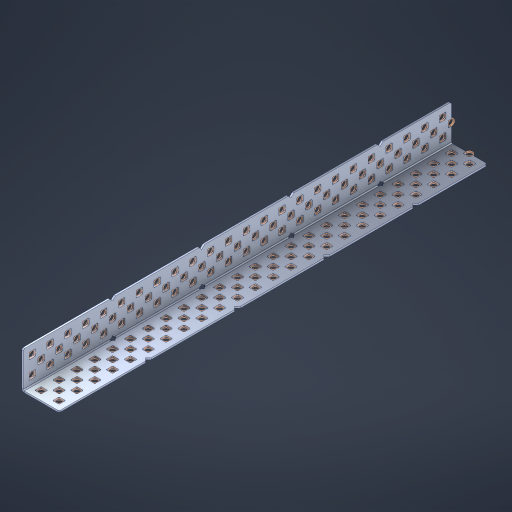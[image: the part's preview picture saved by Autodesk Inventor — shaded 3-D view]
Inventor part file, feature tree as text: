
AUTODESK INVENTOR PART (.ipt)
format: ipt  version: 2023 (Build 270158000, 158)  size: 1,733,120 bytes
history: native  units: in
note: dims shown in document units (in); Inventor stores cm internally (conversion verified against a paired STEP export)
features: other x150, extrude x142, sheet_metal_op x8, sketch x7, pattern_linear x2, mirror x1, chamfer x1
ambient origin geometry x8: Origin, YZ Plane, XZ Plane, XY Plane, X Axis, Y Axis, Z Axis, Center Point
bodies: Solid1 (feature_tree), Body (feature_tree)
feature tree (311):
  sheet_metal_op  "Flanges"
  sheet_metal_op  "Body Pattern"
  pattern_linear  "Center Pattern"  Spacing1=1.0in  [1 undecoded]
  other  "Arc Length"
  pattern_linear  "Notch Pattern"  Spacing1=0.1875in  [1 undecoded]
  other  "Diagonal Plane"
  mirror  "Everything Mirrored"
  chamfer  "End Chamfer"
  sketch  "Sketch1"  dims[d0=1.0in]
  other  "Plate1"
  sketch  "Sketch2"  dims[d1=12.0in]
  other  "Plate2"
  sheet_metal_op  "Bend1"
  sheet_metal_op  "Corner1"
  sketch  "Sketch8"  dims[d2=0.0469in]
  sketch  "Sketch9"  dims[d3=0.0469in]
  other  "Srf91"
  sheet_metal_op  "Body Pattern Sketch"
  other  "Srf92"
  sketch  "Sketch13"  dims[d4=0.0234in]
  sketch  "Sketch15"  dims[d5=0.0938in]
  sketch  "Sketch16"  dims[d6=0.0469in d7=1.0in d8=90.0deg d9=0.0312in d10=0.1875in d11=0.0469in d12=0.0469in d49=0.182in d50=0.02in d52=0.25in d53=0.0469in d54=0.0in d55=0.172in d56=1.0in d57=0.0in d60=9.4488in d62=0.5in d63=0.7874in d65=0.5in d85=0.1473in d86=0.1659in d89=0.0469in d90=0.0in d91=0.04in d92=0.0491in d95=2.5in d96=0.04in d97=0.25in d98=45.0deg d99=0.25in d106=0.182in d107=0.02in d108=0.5in d110=0.0469in d111=0.0in d112=0.172in d113=0.5in d114=0.0in d117=0.5in d123=0.25in d125=0.25in d126=0.0491in d127=0.1227in d128=0.08in d129=0.04in d130=2.5in]
  other  "Srf786"
  other  "Srf856"
  other  "Srf857"
  other  "Srf858"
  other  "Srf859"
  other  "Srf860"
  other  "Srf861"
  other  "Srf889"
  other  "Srf890"
  other  "Srf891"
  other  "Srf1275"
  other  "Srf1276"
  other  "Srf1278"
  other  "Srf1279"
  other  "Srf1280"
  other  "Srf1281"
  other  "Srf1282"
  other  "Srf1283"
  other  "Srf1277"
  other  "Srf1285"
  other  "Srf1286"
  other  "Srf1287"
  other  "Srf1383"
  other  "Srf1384"
  other  "Srf1385"
  other  "Srf1386"
  other  "Srf1387"
  other  "Srf1388"
  other  "Srf1389"
  other  "Srf1390"
  other  "Srf1391"
  other  "Srf1392"
  other  "Srf1393"
  other  "Srf1394"
  other  "Srf1395"
  other  "Srf1396"
  other  "Srf1397"
  other  "Srf1398"
  other  "Srf1399"
  other  "Srf1400"
  other  "Srf1401"
  other  "Srf1402"
  other  "Srf1403"
  other  "Srf1404"
  other  "Srf1405"
  other  "Srf1406"
  other  "Srf1407"
  other  "Srf1408"
  other  "Srf1409"
  other  "Srf1410"
  other  "Srf1411"
  other  "Srf1412"
  other  "Srf1413"
  other  "Srf1414"
  other  "Srf1415"
  other  "Srf1416"
  other  "Srf1417"
  other  "Srf1418"
  other  "Srf1419"
  other  "Srf1420"
  other  "Srf1421"
  other  "Srf1422"
  other  "Srf1445"
  other  "Srf1446"
  other  "Srf1447"
  other  "Srf1448"
  other  "Srf1449"
  other  "Srf1450"
  other  "Srf1451"
  other  "Srf1452"
  other  "Srf1453"
  other  "Srf1454"
  other  "Srf1455"
  other  "Srf1456"
  other  "Srf1457"
  other  "Srf1458"
  other  "Srf1459"
  other  "Srf1460"
  other  "Srf1461"
  other  "Srf1462"
  other  "Srf1463"
  other  "Srf1464"
  other  "Srf1475"
  other  "Srf1476"
  other  "Srf1477"
  other  "Srf1478"
  other  "Srf1479"
  other  "Srf1480"
  other  "Srf1481"
  other  "Srf1482"
  other  "Srf1483"
  other  "Srf1484"
  other  "Srf1485"
  other  "Srf1486"
  other  "Srf1487"
  other  "Srf1488"
  other  "Srf1489"
  other  "Srf1490"
  other  "Srf1491"
  other  "Srf1492"
  other  "Srf1493"
  other  "Srf1494"
  other  "Srf1495"
  other  "Srf1496"
  other  "Srf1497"
  other  "Srf1498"
  other  "Srf1499"
  other  "Srf1500"
  other  "Srf1501"
  other  "Srf1502"
  other  "Srf1503"
  other  "Srf1504"
  other  "Srf1505"
  other  "Srf1506"
  other  "Srf1507"
  other  "Srf1508"
  other  "Srf1509"
  other  "Srf1510"
  other  "Srf1511"
  other  "Srf1512"
  other  "Srf1513"
  other  "Srf1514"
  other  "Srf1537"
  other  "Srf1538"
  other  "Srf1539"
  other  "Srf1540"
  other  "Srf1541"
  other  "Srf1542"
  other  "Srf1543"
  other  "Srf1544"
  other  "Srf1545"
  other  "Srf1546"
  other  "Srf1547"
  other  "Srf1548"
  other  "Srf1549"
  other  "Srf1550"
  other  "Srf1551"
  other  "Srf1552"
  other  "Srf1553"
  other  "Srf1554"
  other  "Srf1555"
  other  "Srf1556"
  sheet_metal_op  "Body Stamp"
  sheet_metal_op  "Body Circle"
  other  "Center Stamp"
  other  "Center Circle"
  sheet_metal_op  "Notch"
  extrude  "ExtrusionSrf92"  Depth=0.0469in
  extrude  "ExtrusionSrf856"  Depth=0.0469in
  extrude  "ExtrusionSrf857"  Depth=0.182in
  extrude  "ExtrusionSrf858"  Depth=0.02in
  extrude  "ExtrusionSrf859"  Depth=0.25in
  extrude  "ExtrusionSrf860"  Depth=0.0469in
  extrude  "ExtrusionSrf861"  TaperAngle=0.0deg  [1 undecoded]
  extrude  "ExtrusionSrf889"  Depth=2.5in
  extrude  "ExtrusionSrf890"  Depth=1.0in TaperAngle=0.0deg
  extrude  "ExtrusionSrf891"  Depth=2.5in
  extrude  "ExtrusionSrf1275"  Depth=0.5in
  extrude  "ExtrusionSrf1276"  Depth=2.5in
  extrude  "ExtrusionSrf1277"  Depth=2.5in
  extrude  "ExtrusionSrf1278"  Depth=0.0469in
  extrude  "ExtrusionSrf1279"  Depth=2.5in TaperAngle=0.0deg
  extrude  "ExtrusionSrf1280"  Depth=2.5in
  extrude  "ExtrusionSrf1281"  Depth=0.25in TaperAngle=45.0deg
  extrude  "ExtrusionSrf1282"  Depth=0.25in
  extrude  "ExtrusionSrf1345"  Depth=0.182in
  extrude  "ExtrusionSrf1346"  Depth=0.02in
  extrude  "ExtrusionSrf1347"  Depth=0.5in
  extrude  "ExtrusionSrf1348"  Depth=0.0469in
  extrude  "ExtrusionSrf1383"  TaperAngle=0.0deg  [1 undecoded]
  extrude  "ExtrusionSrf1384"  Depth=2.5in
  extrude  "ExtrusionSrf1385"  Depth=0.5in TaperAngle=0.0deg
  extrude  "ExtrusionSrf1386"  Depth=0.5in
  extrude  "ExtrusionSrf1387"  Depth=0.25in
  extrude  "ExtrusionSrf1388"  Depth=0.25in
  extrude  "ExtrusionSrf1389"  Depth=2.5in
  extrude  "ExtrusionSrf1390"  Depth=2.5in
  extrude  "ExtrusionSrf1391"  Depth=2.5in
  extrude  "ExtrusionSrf1392"  Depth=2.5in
  extrude  "ExtrusionSrf1393"  Depth=2.5in
  extrude  "ExtrusionSrf1394"  [1 undecoded]
  extrude  "ExtrusionSrf1395"  [1 undecoded]
  extrude  "ExtrusionSrf1396"  [1 undecoded]
  extrude  "ExtrusionSrf1397"  [1 undecoded]
  extrude  "ExtrusionSrf1398"  [1 undecoded]
  extrude  "ExtrusionSrf1399"  [1 undecoded]
  extrude  "ExtrusionSrf1400"  [1 undecoded]
  extrude  "ExtrusionSrf1401"  [1 undecoded]
  extrude  "ExtrusionSrf1402"  [1 undecoded]
  extrude  "ExtrusionSrf1403"  [1 undecoded]
  extrude  "ExtrusionSrf1404"  [1 undecoded]
  extrude  "ExtrusionSrf1405"  [1 undecoded]
  extrude  "ExtrusionSrf1406"  [1 undecoded]
  extrude  "ExtrusionSrf1407"  [1 undecoded]
  extrude  "ExtrusionSrf1408"  [1 undecoded]
  extrude  "ExtrusionSrf1409"  [1 undecoded]
  extrude  "ExtrusionSrf1410"  [1 undecoded]
  extrude  "ExtrusionSrf1411"  [1 undecoded]
  extrude  "ExtrusionSrf1412"  [1 undecoded]
  extrude  "ExtrusionSrf1413"  [1 undecoded]
  extrude  "ExtrusionSrf1414"  [1 undecoded]
  extrude  "ExtrusionSrf1415"  [1 undecoded]
  extrude  "ExtrusionSrf1416"  [1 undecoded]
  extrude  "ExtrusionSrf1417"  [1 undecoded]
  extrude  "ExtrusionSrf1418"  [1 undecoded]
  extrude  "ExtrusionSrf1419"  [1 undecoded]
  extrude  "ExtrusionSrf1420"  [1 undecoded]
  extrude  "ExtrusionSrf1421"  [1 undecoded]
  extrude  "ExtrusionSrf1422"  [1 undecoded]
  extrude  "ExtrusionSrf1445"  [1 undecoded]
  extrude  "ExtrusionSrf1446"  [1 undecoded]
  extrude  "ExtrusionSrf1447"  [1 undecoded]
  extrude  "ExtrusionSrf1448"  [1 undecoded]
  extrude  "ExtrusionSrf1449"  [1 undecoded]
  extrude  "ExtrusionSrf1450"  [1 undecoded]
  extrude  "ExtrusionSrf1451"  [1 undecoded]
  extrude  "ExtrusionSrf1452"  [1 undecoded]
  extrude  "ExtrusionSrf1453"  [1 undecoded]
  extrude  "ExtrusionSrf1454"  [1 undecoded]
  extrude  "ExtrusionSrf1455"  [1 undecoded]
  extrude  "ExtrusionSrf1456"  [1 undecoded]
  extrude  "ExtrusionSrf1457"  [1 undecoded]
  extrude  "ExtrusionSrf1458"  [1 undecoded]
  extrude  "ExtrusionSrf1459"  [1 undecoded]
  extrude  "ExtrusionSrf1460"  [1 undecoded]
  extrude  "ExtrusionSrf1461"  [1 undecoded]
  extrude  "ExtrusionSrf1462"  [1 undecoded]
  extrude  "ExtrusionSrf1463"  [1 undecoded]
  extrude  "ExtrusionSrf1464"  [1 undecoded]
  extrude  "ExtrusionSrf1475"  [1 undecoded]
  extrude  "ExtrusionSrf1476"  [1 undecoded]
  extrude  "ExtrusionSrf1477"  [1 undecoded]
  extrude  "ExtrusionSrf1478"  [1 undecoded]
  extrude  "ExtrusionSrf1479"  [1 undecoded]
  extrude  "ExtrusionSrf1480"  [1 undecoded]
  extrude  "ExtrusionSrf1481"  [1 undecoded]
  extrude  "ExtrusionSrf1482"  [1 undecoded]
  extrude  "ExtrusionSrf1483"  [1 undecoded]
  extrude  "ExtrusionSrf1484"  [1 undecoded]
  extrude  "ExtrusionSrf1485"  [1 undecoded]
  extrude  "ExtrusionSrf1486"  [1 undecoded]
  extrude  "ExtrusionSrf1487"  [1 undecoded]
  extrude  "ExtrusionSrf1488"  [1 undecoded]
  extrude  "ExtrusionSrf1489"  [1 undecoded]
  extrude  "ExtrusionSrf1490"  [1 undecoded]
  extrude  "ExtrusionSrf1491"  [1 undecoded]
  extrude  "ExtrusionSrf1492"  [1 undecoded]
  extrude  "ExtrusionSrf1493"  [1 undecoded]
  extrude  "ExtrusionSrf1494"  [1 undecoded]
  extrude  "ExtrusionSrf1495"  [1 undecoded]
  extrude  "ExtrusionSrf1496"  [1 undecoded]
  extrude  "ExtrusionSrf1497"  [1 undecoded]
  extrude  "ExtrusionSrf1498"  [1 undecoded]
  extrude  "ExtrusionSrf1499"  [1 undecoded]
  extrude  "ExtrusionSrf1500"  [1 undecoded]
  extrude  "ExtrusionSrf1501"  [1 undecoded]
  extrude  "ExtrusionSrf1502"  [1 undecoded]
  extrude  "ExtrusionSrf1503"  [1 undecoded]
  extrude  "ExtrusionSrf1504"  [1 undecoded]
  extrude  "ExtrusionSrf1505"  [1 undecoded]
  extrude  "ExtrusionSrf1506"  [1 undecoded]
  extrude  "ExtrusionSrf1507"  [1 undecoded]
  extrude  "ExtrusionSrf1508"  [1 undecoded]
  extrude  "ExtrusionSrf1509"  [1 undecoded]
  extrude  "ExtrusionSrf1510"  [1 undecoded]
  extrude  "ExtrusionSrf1511"  [1 undecoded]
  extrude  "ExtrusionSrf1512"  [1 undecoded]
  extrude  "ExtrusionSrf1513"  [1 undecoded]
  extrude  "ExtrusionSrf1514"  [1 undecoded]
  extrude  "ExtrusionSrf1537"  [1 undecoded]
  extrude  "ExtrusionSrf1538"  [1 undecoded]
  extrude  "ExtrusionSrf1539"  [1 undecoded]
  extrude  "ExtrusionSrf1540"  [1 undecoded]
  extrude  "ExtrusionSrf1541"  [1 undecoded]
  extrude  "ExtrusionSrf1542"  [1 undecoded]
  extrude  "ExtrusionSrf1543"  [1 undecoded]
  extrude  "ExtrusionSrf1544"  [1 undecoded]
  extrude  "ExtrusionSrf1545"  [1 undecoded]
  extrude  "ExtrusionSrf1546"  [1 undecoded]
  extrude  "ExtrusionSrf1547"  [1 undecoded]
  extrude  "ExtrusionSrf1548"  [1 undecoded]
  extrude  "ExtrusionSrf1549"  [1 undecoded]
  extrude  "ExtrusionSrf1550"  [1 undecoded]
  extrude  "ExtrusionSrf1551"  [1 undecoded]
  extrude  "ExtrusionSrf1552"  [1 undecoded]
  extrude  "ExtrusionSrf1553"  [1 undecoded]
  extrude  "ExtrusionSrf1554"  [1 undecoded]
  extrude  "ExtrusionSrf1555"  [1 undecoded]
  extrude  "ExtrusionSrf1556"  [1 undecoded]
note: 113 required parameter values undecoded (feature->parameter linkage not recoverable at this tier; creation-order binding heuristic only, values carry confidence <= 0.55)
